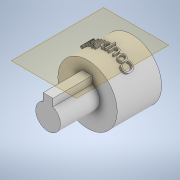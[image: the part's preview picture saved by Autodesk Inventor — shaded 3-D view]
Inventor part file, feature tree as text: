
AUTODESK INVENTOR PART (.ipt)
format: ipt  version: 2021 (Build 250183000, 183)  size: 441,344 bytes
history: native  units: mm
features: sketch x7, extrude x4, loft x1, plane x1, emboss x1
ambient origin geometry x8: Origin, YZ Plane, XZ Plane, XY Plane, X Axis, Y Axis, Z Axis, Center Point
bodies: Body1 (feature_tree)
feature tree (14):
  extrude  "Extrusion4"  Depth=7.0mm TaperAngle=0.0deg
  loft  "Loft3"
  extrude  "Extrusion5"  Depth=2.5mm
  extrude  "Extrusion6"  Depth=6.0mm
  extrude  "Extrusion8"  Depth=3.0mm
  plane  "Work Plane4"
  emboss  "Emboss1"
  sketch  "Sketch8"  dims[d35=12.0mm d36=7.0mm d37=0.0mm]
  sketch  "Sketch9"  dims[d38=5.0mm d39=5.0mm]
  sketch  "Sketch10"  dims[d40=2.5mm d41=2.5mm]
  sketch  "Sketch11"  dims[d42=6.0mm d43=6.0mm]
  sketch  "Sketch12"  dims[d44=3.0mm d45=3.0mm]
  sketch  "Sketch14"  dims[d46=0.0mm d47=90.0deg]
  sketch  "Sketch16"  dims[d48=0.0mm d49=90.0deg d50=2.0mm d51=0.0mm d52=5.0mm d53=8.0mm d54=0.0mm d57=2.0mm d58=1.5mm d59=1.0mm d60=8.0mm d61=0.0mm d63=7.0mm d64=0.5mm d65=0.0mm d22=0.5mm d23=0.872665mm d24=0.5mm d25=0.872665mm]
